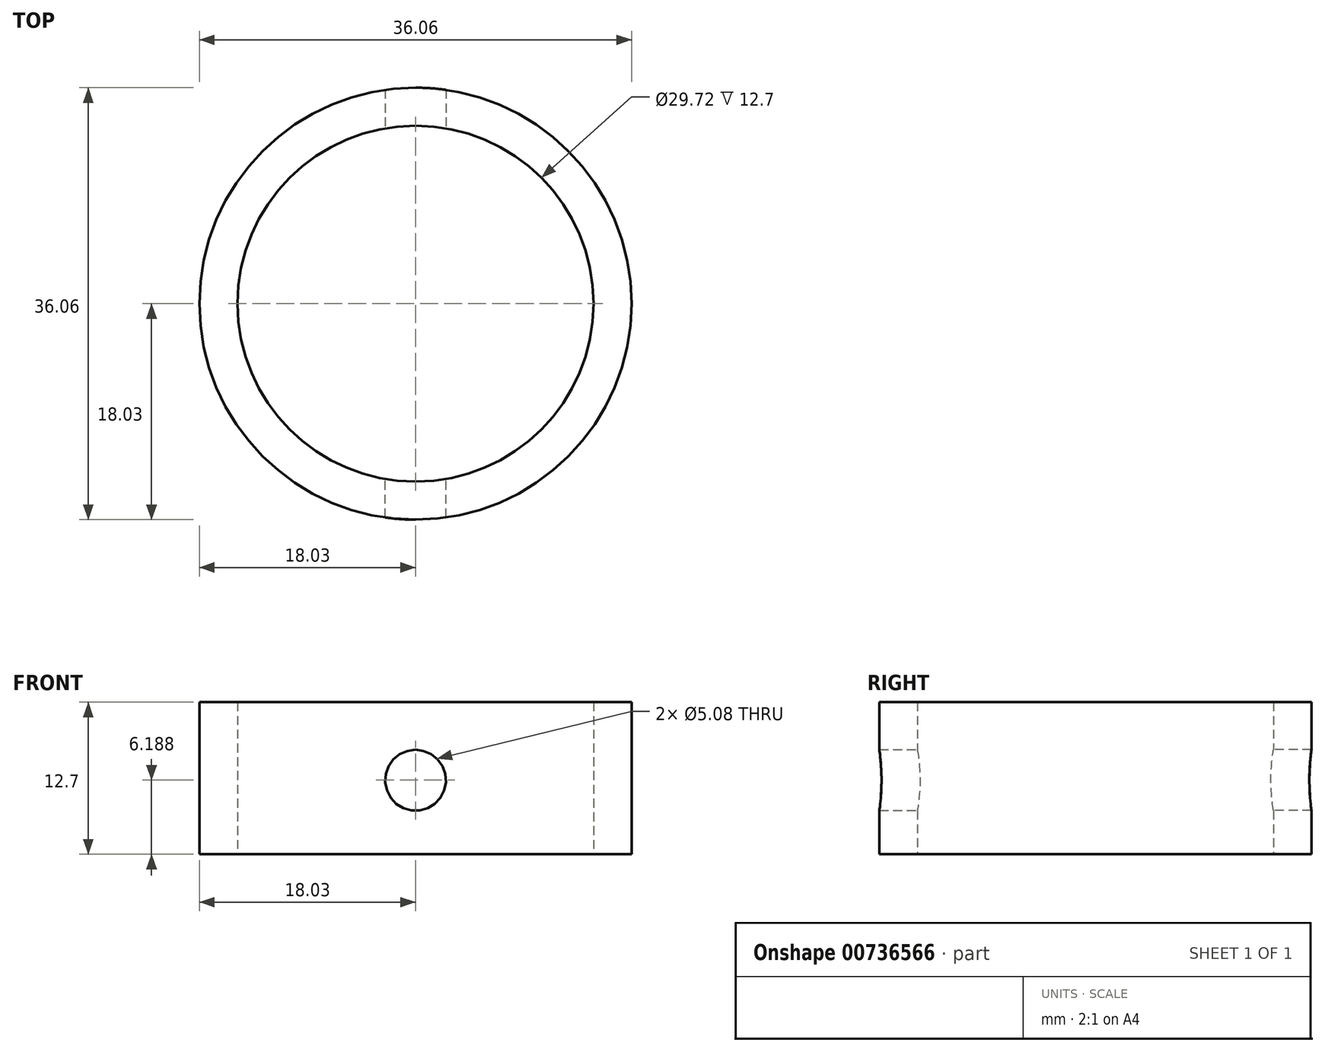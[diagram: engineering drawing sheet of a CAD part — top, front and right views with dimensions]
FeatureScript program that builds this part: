
annotation { "Feature Type Name" : "Feature", "Feature Type Description" : "" }
export const myFeature = defineFeature(function(context is Context, id is Id, definition is map)
    precondition{}
    {
        {
            var Q0;
            Q0=qCreatedBy(makeId("Top.planeOp"),FACE);
            var sketch = newSketch(context, id + "F0", { "sketchPlane" : qUnion([Q0])});
            skCircle(sketch, "E0", {"center": v(0, 0) * mm, "radius": 18.03 * mm});
            skCircle(sketch, "E1.0", {"center": v(0, 0) * mm, "radius": 14.86 * mm});
            skSolve(sketch);
        }
        {
            var Q0;
            Q0 = qSketchRegion(id + "F0", true);
            extrude(context, id + "F1", {"entities" : qUnion([Q0]), "depth" : 12.7 * mm, "offsetDistance" : 25.4 * mm});
        }
        {
            var Q0;
            Q0=qCreatedBy(makeId("Front.planeOp"),FACE);
            var sketch = newSketch(context, id + "F2", { "sketchPlane" : qUnion([Q0])});
            skCircle(sketch, "E2", {"center": v(0, 6.19) * mm, "radius": 2.54 * mm});
            skPoint(sketch, "E3.end.orphan", {"position": v(22.66, 0) * mm});
            skPoint(sketch, "E4.end.orphan", {"position": v(-18.13, 0) * mm});
            skLineSegment(sketch, "E5.bottom", {"start": v(18.13, 12.66) * mm, "end": v(-18.13, 12.66) * mm, "construction": true});
            skLineSegment(sketch, "E5.top", {"start": v(18.13, 0) * mm, "end": v(-18.13, 0) * mm, "construction": true});
            skLineSegment(sketch, "E5.left", {"start": v(18.13, 12.66) * mm, "end": v(18.13, 0) * mm, "construction": true});
            skLineSegment(sketch, "E5.right", {"start": v(-18.13, 12.66) * mm, "end": v(-18.13, 0) * mm, "construction": true});
            skLineSegment(sketch, "E6", {"start": v(18.13, 6.33) * mm, "end": v(-18.13, 6.19) * mm, "construction": true});
            skLineSegment(sketch, "E7", {"start": v(0, 12.66) * mm, "end": v(0, 0) * mm, "construction": true});
            skSolve(sketch);
        }
        {
            var Q0;
            Q0 = qSketchRegion(id + "F2", true);
            extrude(context, id + "F3", {"entities" : qUnion([Q0]), "operationType" : NewBodyOperationType.REMOVE, "oppositeDirection" : true, "depth" : 50.8 * mm, "offsetDistance" : 25.4 * mm});
        }
        {
            var Q0;
            Q0 = qSketchRegion(id + "F2", true);
            extrude(context, id + "F4", {"entities" : qUnion([Q0]), "operationType" : NewBodyOperationType.REMOVE, "depth" : 50.8 * mm, "offsetDistance" : 25.4 * mm});
        }
    });
